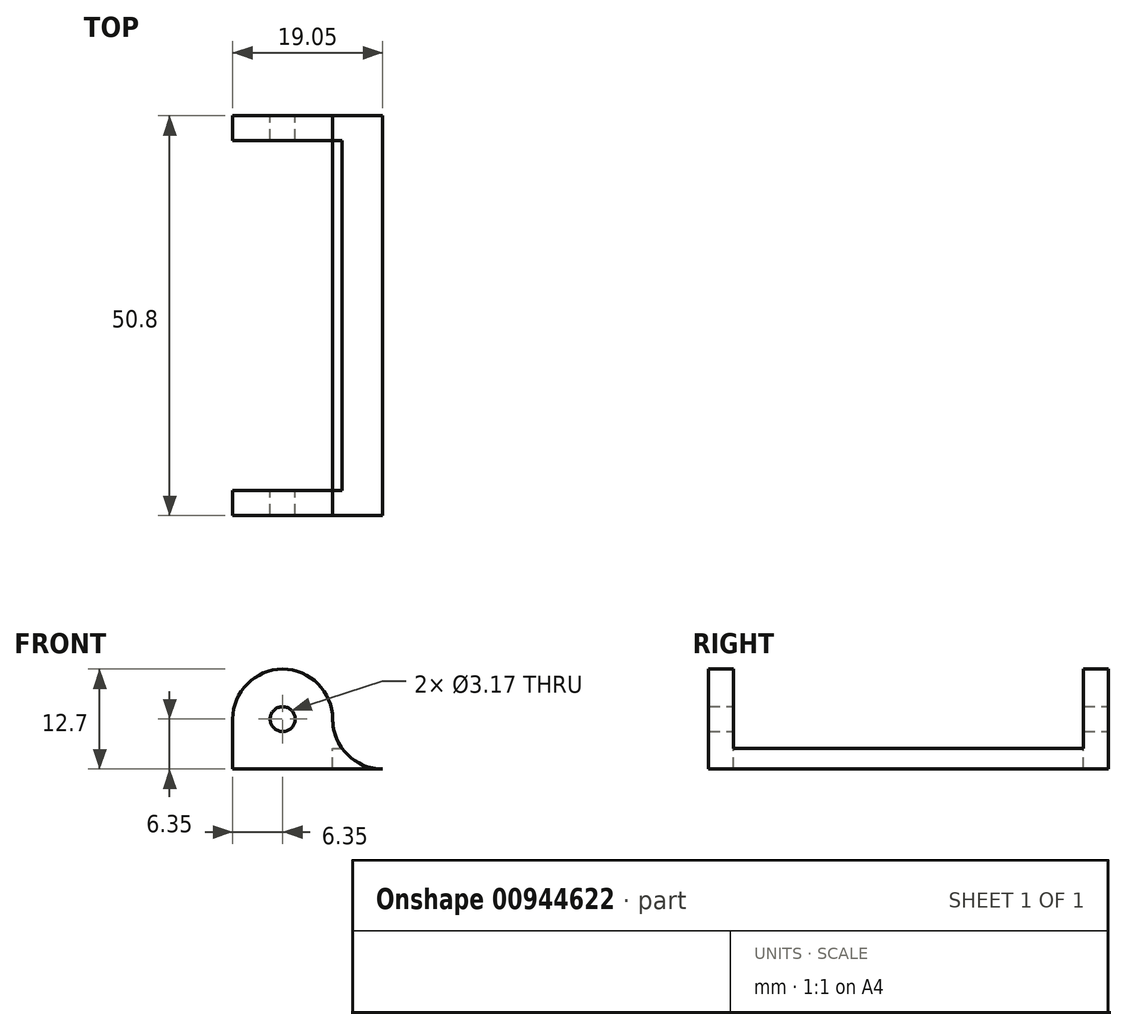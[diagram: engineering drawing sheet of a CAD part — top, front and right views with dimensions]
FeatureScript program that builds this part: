
annotation { "Feature Type Name" : "Feature", "Feature Type Description" : "" }
export const myFeature = defineFeature(function(context is Context, id is Id, definition is map)
    precondition{}
    {
        {
            var Q0;
            Q0=qCreatedBy(makeId("Front.planeOp"),FACE);
            var sketch = newSketch(context, id + "F0", { "sketchPlane" : qUnion([Q0])});
            skLineSegment(sketch, "E0.top", {"start": v(6.35, -6.35) * mm, "end": v(-12.7, -6.35) * mm});
            skLineSegment(sketch, "E0.right", {"start": v(-12.7, 0) * mm, "end": v(-12.7, -6.35) * mm});
            skPoint(sketch, "E0.middle", {"position": v(0, 0) * mm});
            skLineSegment(sketch, "E1", {"start": v(0, -6.35) * mm, "end": v(-12.7, -6.35) * mm});
            skCircle(sketch, "E2", {"center": v(-6.35, 0) * mm, "radius": 1.59 * mm});
            skArc(sketch, "E3", {"start": v(0, 0) * mm, "mid": v(-6.35, 6.35) * mm, "end": v(-12.7, 0) * mm});
            skArc(sketch, "E4", {"start": v(0, 0) * mm, "mid": v(1.86, -4.5) * mm, "end": v(6.35, -6.35) * mm});
            skPoint(sketch, "E5.orphan", {"position": v(12.7, 0) * mm});
            skPoint(sketch, "E6.orphan", {"position": v(12.7, -6.35) * mm});
            skPoint(sketch, "E7.orphan", {"position": v(12.7, 6.35) * mm});
            skPoint(sketch, "E8.orphan", {"position": v(0, 6.35) * mm});
            skPoint(sketch, "E9.orphan", {"position": v(-12.7, 6.35) * mm});
            skPoint(sketch, "E10.orphan", {"position": v(-6.35, 6.35) * mm});
            skPoint(sketch, "E11.start.orphan", {"position": v(-6.35, -6.35) * mm});
            skSolve(sketch);
        }
        {
            var Q0;
            {var subQ0=sQuery(id+"F0.wireOp",EDGE,"E0.right");Q0=makeQuery(id+"F0.imprint","IMPRINT",FACE,{"disambiguationData":[TD([[makeQuery(id+"F0.imprint","IMPRINT",EDGE,{"derivedFrom":subQ0}),1.0]])]});}
            extrude(context, id + "F1", {"entities" : qUnion([Q0]), "endBound" : BoundingType.SYMMETRIC, "depth" : 50.8 * mm, "offsetDistance" : 25.4 * mm});
        }
        {
            var Q0;
            Q0=qCreatedBy(makeId("Right.planeOp"),FACE);
            var sketch = newSketch(context, id + "F2", { "sketchPlane" : qUnion([Q0])});
            skLineSegment(sketch, "E12.bottom", {"start": v(-22.23, 7.4) * mm, "end": v(22.23, 7.4) * mm});
            skLineSegment(sketch, "E12.left", {"start": v(-22.23, 7.4) * mm, "end": v(-22.23, -3.7) * mm});
            skLineSegment(sketch, "E12.right", {"start": v(22.23, 7.4) * mm, "end": v(22.23, -3.7) * mm});
            skPoint(sketch, "E12.middle", {"position": v(0, 0) * mm});
            skLineSegment(sketch, "E13.0", {"start": v(-22.23, -3.7) * mm, "end": v(22.23, -3.7) * mm});
            skPoint(sketch, "E14.orphan", {"position": v(22.23, -7.4) * mm});
            skPoint(sketch, "E15.orphan", {"position": v(-22.23, -7.4) * mm});
            skSolve(sketch);
        }
        {
            var Q0;
            Q0 = qSketchRegion(id + "F2", true);
            extrude(context, id + "F3", {"entities" : qUnion([Q0]), "operationType" : NewBodyOperationType.REMOVE, "endBound" : BoundingType.SYMMETRIC, "oppositeDirection" : true, "depth" : 50.8 * mm, "offsetDistance" : 25.4 * mm});
        }
        {
            var Q0;
            Q0=makeQuery(id+"F3.boolean.opBoolean","COPY",FACE,{"derivedFrom":makeQuery(id+"F3.opExtrude","SWEPT_FACE",FACE,{"disambiguationData":[OSD([sQuery(id+"F2.wireOp",EDGE,"E13.0")])]})});
            var sketch = newSketch(context, id + "F4", { "sketchPlane" : qUnion([Q0])});
            skLineSegment(sketch, "E16.bottom", {"start": v(-12.7, 22.23) * mm, "end": v(0, 22.23) * mm});
            skLineSegment(sketch, "E16.top", {"start": v(-12.7, -22.23) * mm, "end": v(0, -22.23) * mm});
            skLineSegment(sketch, "E16.left", {"start": v(-12.7, 22.23) * mm, "end": v(-12.7, -22.23) * mm});
            skLineSegment(sketch, "E16.right", {"start": v(0, 22.23) * mm, "end": v(0, -22.23) * mm});
            skSolve(sketch);
        }
        {
            var Q0;
            Q0 = qSketchRegion(id + "F4", true);
            extrude(context, id + "F5", {"entities" : qUnion([Q0]), "operationType" : NewBodyOperationType.REMOVE, "endBound" : BoundingType.THROUGH_ALL, "oppositeDirection" : true, "depth" : 25.4 * mm, "offsetDistance" : 25.4 * mm});
        }
    });
